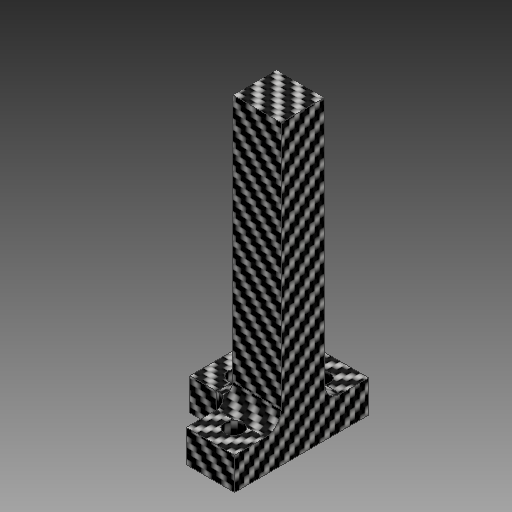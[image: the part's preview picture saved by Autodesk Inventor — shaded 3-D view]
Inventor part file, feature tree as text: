
AUTODESK INVENTOR PART (.ipt)
format: ipt  version: 2018 (Build 220112000, 112)  size: 295,424 bytes
history: native  units: mm
features: extrude x5, sketch x5, other x4, projected_geometry x3, reference x2, fillet x1
ambient origin geometry x8: Origin, YZ Plane, XZ Plane, XY Plane, X Axis, Y Axis, Z Axis, Center Point
bodies: Volumenkörper1 (feature_tree)
feature tree (20):
  extrude  "Extrusion1"  Depth=25.0mm
  extrude  "Extrusion2"  Depth=4.5mm
  extrude  "Extrusion3"  Depth=8.0mm
  fillet  "Rundung2"  Radius=75.0mm
  extrude  "Extrusion4"  Depth=75.0mm TaperAngle=0.0deg
  extrude  "Extrusion5"  Depth=10.0mm
  sketch  "Skizze1"  dims[d0=9.0mm d1=25.0mm]
  reference  "Referenz1"
  sketch  "Skizze2"  dims[d2=4.5mm d3=4.5mm]
  projected_geometry  "Projizierte Kontur1"
  projected_geometry  "Projizierte Kontur2"
  sketch  "Skizze3"  dims[d4=25.0mm d5=8.0mm d6=75.0mm d7=0.0mm]
  projected_geometry  "Projizierte Kontur3"
  reference  "Referenz2"
  sketch  "Skizze4"  dims[d8=6.0mm d9=75.0mm d10=0.0mm]
  sketch  "Skizze5"  dims[d12=75.0mm d13=0.0mm d14=5.2mm d16=3.0mm d17=10.0mm d18=0.0mm d19=10.0mm d20=0.0mm d21=3.4mm]
  other  "<userpath>\OneDrive\Development\Mohne\03_Konstruktion\Mohne komplett.iam"
  other  "Mohne komplett.iam"
  other  "chassis mit motorlöcher:1"
  other  "Wheel ALL1_MIR:1"
